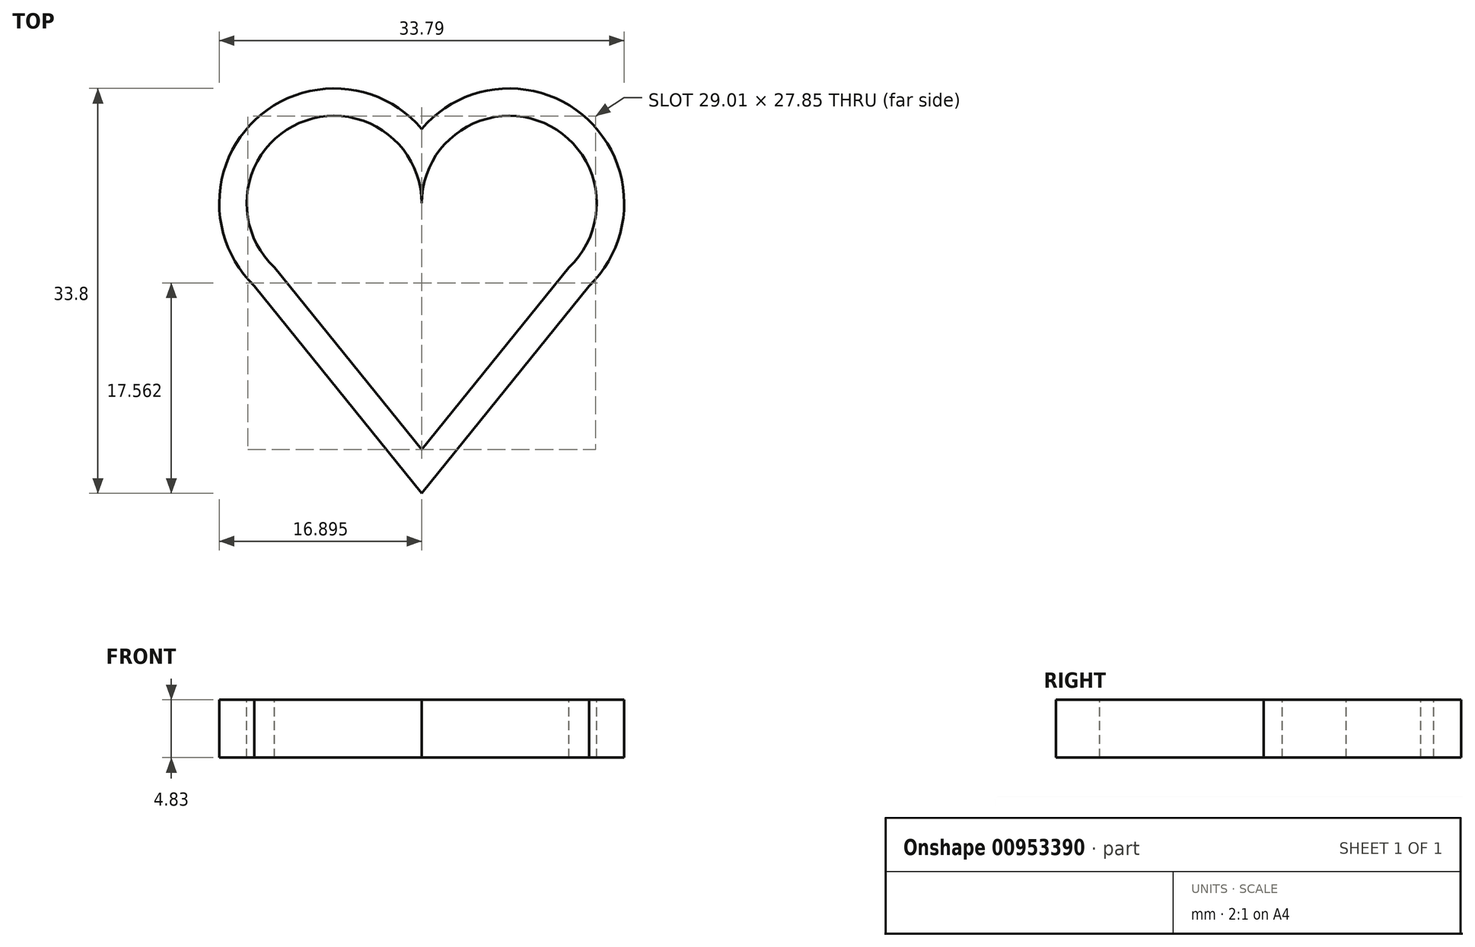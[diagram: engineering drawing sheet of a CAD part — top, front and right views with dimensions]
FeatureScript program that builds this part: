
annotation { "Feature Type Name" : "Feature", "Feature Type Description" : "" }
export const myFeature = defineFeature(function(context is Context, id is Id, definition is map)
    precondition{}
    {
        {
            var Q0;
            Q0=qCreatedBy(makeId("Top.planeOp"),FACE);
            var sketch = newSketch(context, id + "F0", { "sketchPlane" : qUnion([Q0])});
            skArc(sketch, "E0", {"start": v(7.3, 0) * mm, "mid": v(-2.91, 6.7) * mm, "end": v(-4.98, -5.34) * mm});
            skLineSegment(sketch, "E1", {"start": v(7.3, -20.57) * mm, "end": v(-4.98, -5.34) * mm});
            skArc(sketch, "E2.MirrorC", {"start": v(7.3, 0) * mm, "mid": v(17.52, 6.7) * mm, "end": v(19.6, -5.34) * mm});
            skLineSegment(sketch, "E3.MirrorCS", {"start": v(7.3, -20.57) * mm, "end": v(19.6, -5.34) * mm});
            skSolve(sketch);
        }
        {
            var Q0;
            Q0=makeQuery(id+"F0.imprint","IMPRINT",FACE,{"disambiguationData":[TD([[makeQuery(id+"F0.imprint","IMPRINT",EDGE,{"derivedFrom":sQuery(id+"F0.wireOp",EDGE,"E0")}),1.0]])]});
            extrude(context, id + "F1", {"entities" : qUnion([Q0]), "depth" : 2.3 * mm, "offsetDistance" : 25.4 * mm});
        }
        {
            var Q0;
            Q0=makeQuery(id+"F1.opExtrude","CAP_FACE",FACE,{"disambiguationData":[OSD([sQuery(id+"F0.wireOp",EDGE,"E0"),sQuery(id+"F0.wireOp",EDGE,"E1"),sQuery(id+"F0.wireOp",EDGE,"E2.MirrorC"),sQuery(id+"F0.wireOp",EDGE,"E3.MirrorCS")])],"isStart":false});
            var sketch = newSketch(context, id + "F2", { "sketchPlane" : qUnion([Q0])});
            skLineSegment(sketch, "E4.0", {"start": v(-6.67, -6.9) * mm, "end": v(7.3, -24.21) * mm});
            skArc(sketch, "E4.1", {"start": v(7.3, 6.21) * mm, "mid": v(-6.56, 7) * mm, "end": v(-6.67, -6.9) * mm});
            skArc(sketch, "E4.2", {"start": v(21.28, -6.9) * mm, "mid": v(21.17, 7) * mm, "end": v(7.3, 6.21) * mm});
            skLineSegment(sketch, "E4.3", {"start": v(7.3, -24.21) * mm, "end": v(21.28, -6.9) * mm});
            skSolve(sketch);
        }
        {
            var Q0;
            Q0=makeQuery(id+"F2.imprint","IMPRINT",FACE,{"disambiguationData":[TD([[makeQuery(id+"F2.imprint","IMPRINT",EDGE,{"derivedFrom":sQuery(id+"F2.wireOp",EDGE,"E4.0")}),1.0]])]});
            extrude(context, id + "F3", {"entities" : qUnion([Q0]), "operationType" : NewBodyOperationType.ADD, "oppositeDirection" : true, "depth" : 4.83 * mm, "offsetDistance" : 25.4 * mm});
        }
        {
            var Q0;
            Q0=makeQuery(id+"F1.opExtrude","CAP_FACE",FACE,{"disambiguationData":[OSD([sQuery(id+"F0.wireOp",EDGE,"E0"),sQuery(id+"F0.wireOp",EDGE,"E1"),sQuery(id+"F0.wireOp",EDGE,"E2.MirrorC"),sQuery(id+"F0.wireOp",EDGE,"E3.MirrorCS")])],"isStart":true});
            extrude(context, id + "F4", {"entities" : qUnion([Q0]), "operationType" : NewBodyOperationType.REMOVE, "endBound" : BoundingType.THROUGH_ALL, "oppositeDirection" : true, "depth" : 25.4 * mm, "offsetDistance" : 25.4 * mm});
        }
    });
